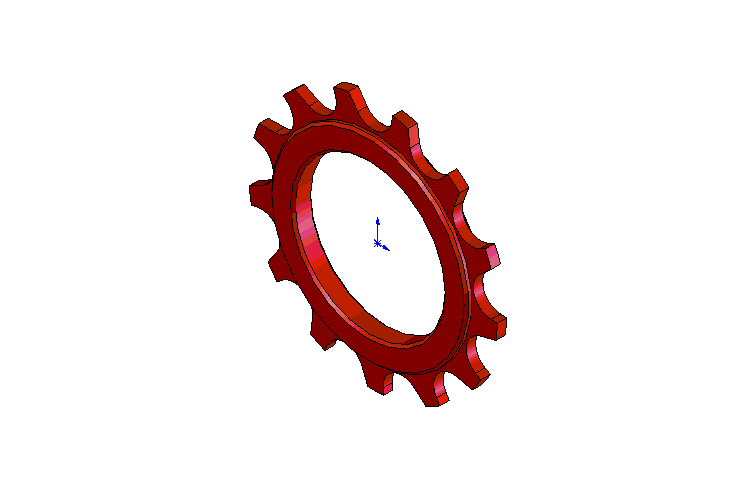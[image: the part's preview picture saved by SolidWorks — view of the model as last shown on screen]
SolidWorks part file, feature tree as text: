
SOLIDWORKS PART (.sldprt)
format: sldprt  version: not decoded by parser v0  size: 244,736 bytes
history: native  units: mm
features: sketch x4, plane x3, extrude x3, material x1, cut_extrude x1, pattern_circular x1, chamfer x1 (+10 scaffold rows collapsed)
feature tree (24):
  scaffold x10  (default folders/planes/origin — collapsed)
  material  "Matériau <non spécifié>"
  plane  "Plan de face"
  plane  "Plan de dessus"
  plane  "Plan de droite"
  sketch  "Esquisse1"  dims[D1=53.0mm]
  extrude  "Extrusion1"  Depth=2mm
  sketch  "Esquisse2"  dims[c1.D1=8.0mm c1.D3=4.0mm c2.D1=8.0mm c2.D3=4.0mm c2.D2=9.5mm c3.D3=4.0mm c3.D2=~2.039916mm c4.D2=35.0deg c4.D3=5.0mm]
  cut_extrude  "Enlèv. mat.-Extru.1"  [1 undecoded]
  pattern_circular  "Répétition circulaire1"  Count=13 Angle=27.692308deg
  sketch  "Esquisse3"  dims[D1=42.0mm]
  extrude  "Extrusion2"  Depth=4.25mm
  sketch  "Esquisse4"  dims[D1=32.0mm]
  extrude  "Enlèv. mat.-Extru.2"  [1 undecoded]
  chamfer  "Chanfrein1"  Distance=0.5mm Angle=45deg
decode coverage: 8 of 10 modeling features carry decoded parameters
note: ~ marks probable driven/reference dimensions
note: 2 parameter values undecoded
note: suppression state not decoded; provenance and decode notes live in map.json
